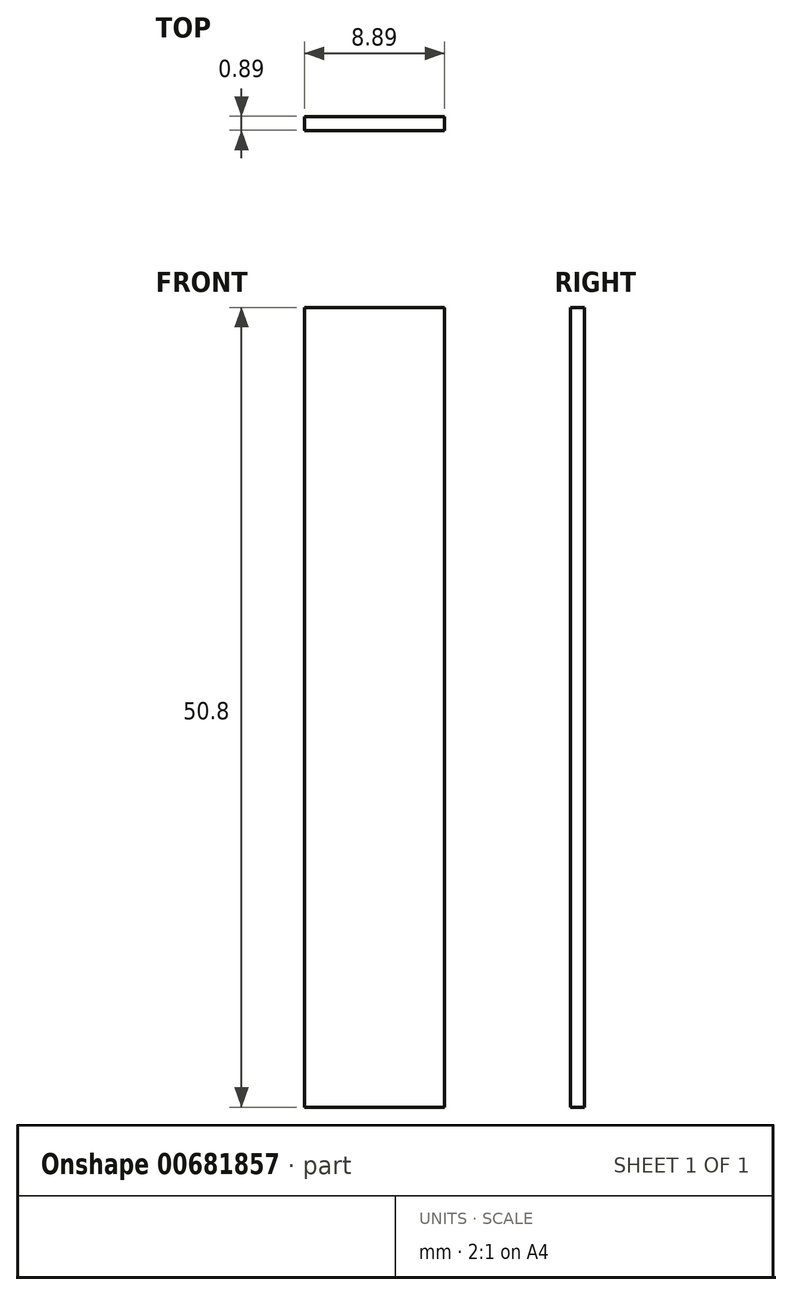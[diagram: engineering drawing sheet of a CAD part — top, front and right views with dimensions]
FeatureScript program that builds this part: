
annotation { "Feature Type Name" : "Feature", "Feature Type Description" : "" }
export const myFeature = defineFeature(function(context is Context, id is Id, definition is map)
    precondition{}
    {
        {
            var Q0;
            Q0=qCreatedBy(makeId("Top.planeOp"),FACE);
            var sketch = newSketch(context, id + "F0", { "sketchPlane" : qUnion([Q0])});
            skLineSegment(sketch, "E0.bottom", {"start": v(101.25, 4.58) * mm, "end": v(92.36, 4.58) * mm});
            skLineSegment(sketch, "E0.top", {"start": v(101.25, 5.47) * mm, "end": v(92.36, 5.47) * mm});
            skLineSegment(sketch, "E0.left", {"start": v(101.25, 4.58) * mm, "end": v(101.25, 5.47) * mm});
            skLineSegment(sketch, "E0.right", {"start": v(92.36, 4.58) * mm, "end": v(92.36, 5.47) * mm});
            skSolve(sketch);
        }
        {
            var Q0;
            Q0 = qSketchRegion(id + "F0", true);
            extrude(context, id + "F1", {"entities" : qUnion([Q0]), "depth" : 50.8 * mm, "offsetDistance" : 25.4 * mm});
        }
    });
